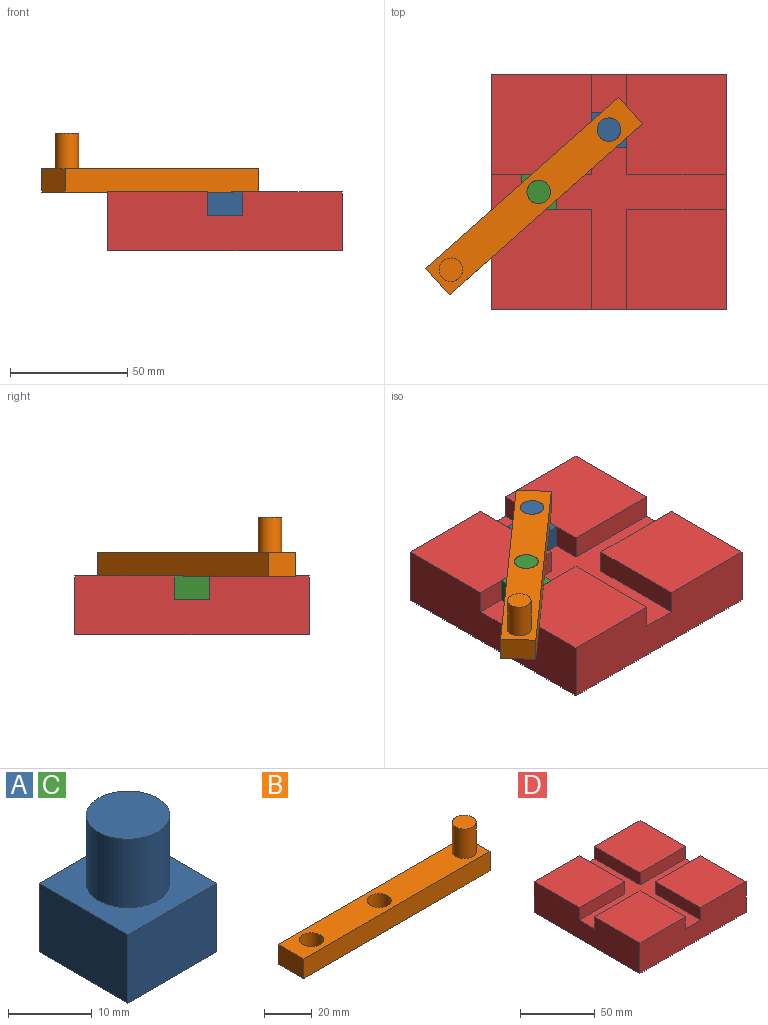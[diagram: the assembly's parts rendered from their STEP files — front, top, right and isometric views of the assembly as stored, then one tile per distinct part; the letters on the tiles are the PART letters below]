
ASSEMBLY  parts=4 mates=4
PART A: 8 faces, bbox 15x15x20 mm
  f0: plane 15x10mm, normal (0,1,0), area 150mm2, adj f1,f3,f4,f5
  f1: plane 15x10mm, normal (-1,0,0), area 150mm2, adj f0,f2,f4,f5
  f2: plane 15x10mm, normal (0,-1,0), area 150mm2, adj f1,f3,f4,f5
  f3: plane 15x10mm, normal (1,0,0), area 150mm2, adj f0,f2,f4,f5
  f4: plane 15x15mm, normal (0,0,1), area 146.5mm2, adj f0,f1,f2,f3,f6
  f5: plane 15x15mm, normal (0,0,-1), area 225mm2, adj f0,f1,f2,f3
  f6: cylinder r=5mm len=10mm, axis (0,0,-1), area 314.2mm2, adj f4,f7
  f7: plane 10x10mm, normal (0,0,1), area 78.5mm2, adj f6
PART B: 10 faces, bbox 110x15x25 mm
  f0: plane 110x10mm, normal (0,1,0), area 1100mm2, adj f1,f5,f6,f7
  f1: plane 15x10mm, normal (-1,0,0), area 150mm2, adj f0,f2,f6,f7
  f2: plane 110x10mm, normal (0,-1,0), area 1100mm2, adj f1,f5,f6,f7
  f3: cylinder r=5mm len=10mm, axis (0,0,-1), area 314.2mm2, adj f6,f7
  f4: cylinder r=5mm len=10mm, axis (0,0,-1), area 314.2mm2, adj f6,f7
  f5: plane 15x10mm, normal (1,0,0), area 150mm2, adj f0,f2,f6,f7
  f6: plane 110x15mm, normal (0,0,1), area 1414.4mm2, adj f0,f1,f2,f3,f4,f5,f8
  f7: plane 110x15mm, normal (0,0,-1), area 1492.9mm2, adj f0,f1,f2,f3,f4,f5
  f8: cylinder r=5mm len=15mm, axis (0,0,-1), area 471.2mm2, adj f6,f9
  f9: plane 10x10mm, normal (0,0,1), area 78.5mm2, adj f8
PART C: same geometry as A
PART D: 18 faces, bbox 100x100x25 mm
  f0: plane 42.5x42.5mm, normal (0,0,1), area 1806.3mm2, adj f1,f3,f6,f17
  f1: plane 100x25mm, normal (-1,0,0), area 2350mm2, adj f0,f5,f6,f7,f10,f12,f16,f17
  f2: plane 42.5x42.5mm, normal (0,0,1), area 1806.3mm2, adj f4,f6,f8,f15
  f3: plane 42.5x10mm, normal (1,0,0), area 425mm2, adj f0,f6,f12,f17
  f4: plane 42.5x10mm, normal (-1,0,0), area 425mm2, adj f2,f6,f12,f15
  f5: plane 42.5x42.5mm, normal (0,0,1), area 1806.3mm2, adj f1,f7,f11,f16
  f6: plane 100x25mm, normal (0,1,0), area 2350mm2, adj f0,f1,f2,f3,f4,f8,f10,f12
  f7: plane 100x25mm, normal (0,-1,0), area 2350mm2, adj f1,f5,f8,f9,f10,f11,f12,f13
  f8: plane 100x25mm, normal (1,0,0), area 2350mm2, adj f2,f6,f7,f9,f10,f12,f14,f15
  f9: plane 42.5x42.5mm, normal (0,0,1), area 1806.3mm2, adj f7,f8,f13,f14
  f10: plane 100x100mm, normal (0,0,-1), area 10000mm2, adj f1,f6,f7,f8
  f11: plane 42.5x10mm, normal (1,0,0), area 425mm2, adj f5,f7,f12,f16
  f12: plane 100x100mm, normal (0,0,1), area 2775mm2, adj f1,f3,f4,f6,f7,f8,f11,f13
  f13: plane 42.5x10mm, normal (-1,0,0), area 425mm2, adj f7,f9,f12,f14
  f14: plane 42.5x10mm, normal (0,1,0), area 425mm2, adj f8,f9,f12,f13
  f15: plane 42.5x10mm, normal (0,-1,0), area 425mm2, adj f2,f4,f8,f12
  f16: plane 42.5x10mm, normal (0,1,0), area 425mm2, adj f1,f5,f11,f12
  f17: plane 42.5x10mm, normal (0,-1,0), area 425mm2, adj f0,f1,f3,f12
PLACE A t=(-46.22,63.24,5.21)mm
PLACE B rot(axis=(0,0,-1),138.4deg) t=(-44.53,-62.44,30.21)mm
PLACE C t=(-76.15,36.7,5.21)mm
PLACE D t=(-46.22,-5.8,5.21)mm fixed
MATE revolute B.f4 <-> C.f6  axis (0,0,1) through (-76.15,-5.8,40.21)mm
MATE slider D.f7 <-> A.f2  axis (0,-1,0) through (-46.22,-55.8,20.21)mm
MATE slider D.f8 <-> C.f3  axis (1,0,0) through (3.78,-5.8,20.21)mm
MATE revolute B.f3 <-> A.f6  axis (0,0,1) through (-46.22,20.74,40.21)mm
